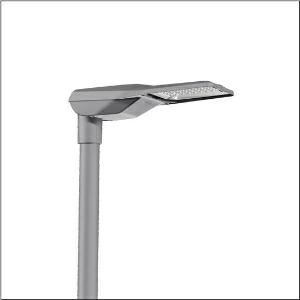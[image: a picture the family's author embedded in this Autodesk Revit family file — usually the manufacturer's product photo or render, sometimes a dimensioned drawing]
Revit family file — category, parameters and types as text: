
# Revit family: streetlight_sl_21_iq_mini___st0_5a_5xe2b41g08gb_465e
name_source: partatom
category: Lighting Fixtures
units: mm (PartAtom-declared; Revit-internal decimal feet)

## family parameters
Cut with Voids When Loaded = No
Host = Face
Light Source = No
Part Type = Normal
Room Calculation Point = No
Round Connector Dimension = Use Diameter
Shared = No

## types (1)
- --- (1 x LED, 5920 lm, 37.1 W, 4000K)
    Apparent Load = 37 VA
    CIE Flux Codes = 41 75 97 100 100
    Color Rendering = 70
    Color Temperature = 4000K
    Default Elevation = 1800 mm
    Description = Streetlight SL 21 iQ mini, mast luminaire, primary light control with lens, of PMMA, primary optical cover: cover, of toughened safety glass, transparent, light distribution: ST0.5a, light emission: direct distribution, primary light characteristic: asymmetric, installation type: post-top, side-entry, LED, High Power LED, rated luminous flux: 5.920lm, luminous efficacy: 160lm/W, light colour: 740, colour temperature: 4000K, control: Street-Remote, Auto-Match, Temp-Guard, Lumen-Switch, Night-Set, Smart-Wire, Light-Fading, Desk-Remote (wireless, voltage-free reading and setting of iQ features in the workshop via application-optimized NFC function/RFID function), optimised constant luminous flux control (CLO 2.0), pre-setting: linear dimming characteristic, mains connection: 220..240V, AC, 50/60Hz, start of lifetime: 37W, end of service life: 39W, reduction: 18W, luminaire housing, of diecast aluminium, powder-coated, Siteco® metallic grey (DB 702S), corrosivity category C5 mid according to DIN EN ISO 12944, please order mast flange separately, inclination adjustable: 0°, 5°, 10°, 15°, sealing non-destructively replaceable, multi-level sealing system, length: 628mm, width: 235mm, height: 110mm, mast flange for spigot size: 42mm (side-entry): 5XC10008XM4, 60/48mm (side-entry/post-top): 5XC10108XM2, 76/60mm (side-entry/post-top): 5XC10108XM1, protection rating (complete): IP66, insulation class (complete): insulation class II (safety insulation), certification: CE, ENEC, ENEC+, VDE, impact resistance: IK09, permissible operating ambient temperature for outdoor applications: -40..+50°C, standard-compliant lighting for roads and squares, packaging unit: 1 piece

Light Distribution: ST0.5a
    Height = 110 mm
    Lamp = 1 x LED
    Lamp Light Flux = 5920 lm
    Lamp Power = 37.1 W
    Lamp count = 1
    Length = 625 mm
    Luminous efficacy = 160 lm/W
    Manufacturer = Siteco
    ModVariant = No
    Model = 5XE2B41G08GB
    Number of Poles = 1
    OnlyDefault = Yes
    Power Factor = 1
    Product Name = Streetlight SL 21 iQ mini | ST0.5a
    Product group = mast luminaire | pylon top
    ProductGroupID = 6100
    Protection Class = Protection class II
    Protection Degree = IP 66
    RLX_Detail_Level = 1
    RLX_Emergency_Light_Flux = 0 lm
    RLX_Emergency_Type = 0
    RLX_Emergency_Type_DB = No
    RlxData = <blob elided: 103117 chars, md5=b8d2c011>
    Socket = socket
    Standby Power = 0 W
    System Light Flux = 5920 lm
    System Power = 37 W
    Type Comments = factory setting: luminous flux: 100 % | dim-lin: 254 | 385 mA
    Type Image = l_1003519.jpg
    URL = http://relux.com
    VarID = @adj_163831
    Voltage = 0 V
    Weight = 0.00 kg
    Width = 234 mm

## geometry (parser evidence)
native form markers: Blend x4, Sweep x12
no freeform markers — native parametric forms only
